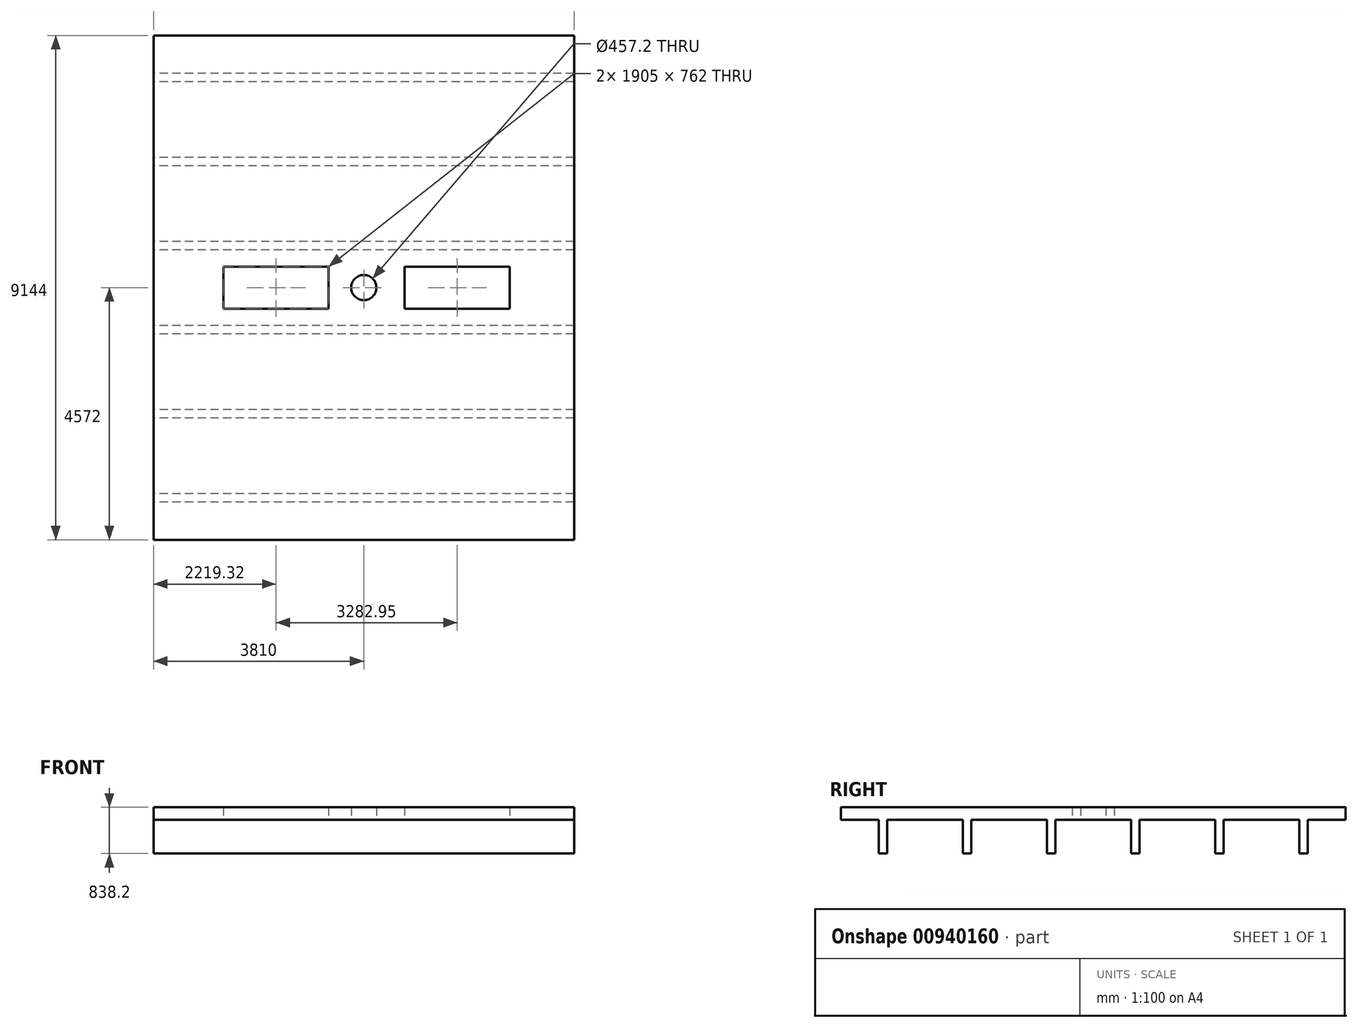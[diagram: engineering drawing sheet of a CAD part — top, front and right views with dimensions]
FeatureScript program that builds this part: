
annotation { "Feature Type Name" : "Feature", "Feature Type Description" : "" }
export const myFeature = defineFeature(function(context is Context, id is Id, definition is map)
    precondition{}
    {
        {
            var Q0;
            Q0=qCreatedBy(makeId("Top.planeOp"),FACE);
            var sketch = newSketch(context, id + "F0", { "sketchPlane" : qUnion([Q0])});
            skLineSegment(sketch, "E0.bottom", {"start": v(-3810, -4572) * mm, "end": v(3810, -4572) * mm});
            skLineSegment(sketch, "E0.top", {"start": v(-3810, 4572) * mm, "end": v(3810, 4572) * mm});
            skLineSegment(sketch, "E0.left", {"start": v(-3810, -4572) * mm, "end": v(-3810, 4572) * mm});
            skLineSegment(sketch, "E0.right", {"start": v(3810, -4572) * mm, "end": v(3810, 4572) * mm});
            skPoint(sketch, "E0.middle", {"position": v(0, 0) * mm});
            skCircle(sketch, "E1", {"center": v(0, 0) * mm, "radius": 228.6 * mm});
            skLineSegment(sketch, "E2.bottom", {"start": v(-2543.18, 381) * mm, "end": v(-638.17, 381) * mm});
            skLineSegment(sketch, "E2.top", {"start": v(-2543.18, -381) * mm, "end": v(-638.17, -381) * mm});
            skLineSegment(sketch, "E2.left", {"start": v(-2543.18, 381) * mm, "end": v(-2543.18, -381) * mm});
            skLineSegment(sketch, "E2.right", {"start": v(-638.18, 381) * mm, "end": v(-638.17, -381) * mm});
            skLineSegment(sketch, "E3.bottom", {"start": v(739.77, 381) * mm, "end": v(2644.78, 381) * mm});
            skLineSegment(sketch, "E3.top", {"start": v(739.78, -381) * mm, "end": v(2644.78, -381) * mm});
            skLineSegment(sketch, "E3.left", {"start": v(739.77, 381) * mm, "end": v(739.78, -381) * mm});
            skLineSegment(sketch, "E3.right", {"start": v(2644.78, 381) * mm, "end": v(2644.78, -381) * mm});
            skLineSegment(sketch, "E4", {"start": v(739.78, 0) * mm, "end": v(0, 0) * mm, "construction": true});
            skLineSegment(sketch, "E5", {"start": v(0, 0) * mm, "end": v(-638.17, 0) * mm, "construction": true});
            skLineSegment(sketch, "E6", {"start": v(0, 0) * mm, "end": v(0, 0) * mm});
            skSolve(sketch);
        }
        {
            var Q0;
            Q0=makeQuery(id+"F0.imprint","IMPRINT",FACE,{"disambiguationData":[TD([[makeQuery(id+"F0.imprint","IMPRINT",EDGE,{"derivedFrom":sQuery(id+"F0.wireOp",EDGE,"E0.bottom")}),1.0]])]});
            extrude(context, id + "F1", {"entities" : qUnion([Q0]), "depth" : 228.6 * mm, "offsetDistance" : 25.4 * mm});
        }
        {
            var Q0;
            Q0=qCreatedBy(makeId("Right.planeOp"),FACE);
            var sketch = newSketch(context, id + "F2", { "sketchPlane" : qUnion([Q0])});
            skLineSegment(sketch, "E7", {"start": v(-685.8, 0) * mm, "end": v(685.8, 0) * mm, "construction": true});
            skLineSegment(sketch, "E8.bottom", {"start": v(-685.8, 0) * mm, "end": v(-838.2, 0) * mm});
            skLineSegment(sketch, "E8.top", {"start": v(-685.8, -609.6) * mm, "end": v(-838.2, -609.6) * mm});
            skLineSegment(sketch, "E8.left", {"start": v(-685.8, 0) * mm, "end": v(-685.8, -609.6) * mm});
            skLineSegment(sketch, "E8.right", {"start": v(-838.2, 0) * mm, "end": v(-838.2, -609.6) * mm});
            skLineSegment(sketch, "E9.bottom", {"start": v(685.8, 0) * mm, "end": v(838.2, 0) * mm});
            skLineSegment(sketch, "E9.top", {"start": v(685.8, -609.6) * mm, "end": v(838.2, -609.6) * mm});
            skLineSegment(sketch, "E9.left", {"start": v(685.8, 0) * mm, "end": v(685.8, -609.6) * mm});
            skLineSegment(sketch, "E9.right", {"start": v(838.2, 0) * mm, "end": v(838.2, -609.6) * mm});
            skLineSegment(sketch, "E10.1.0.0", {"start": v(2362.2, 0) * mm, "end": v(2209.8, 0) * mm});
            skLineSegment(sketch, "E10.1.0.1", {"start": v(2209.8, 0) * mm, "end": v(2209.8, -609.6) * mm});
            skLineSegment(sketch, "E10.1.0.2", {"start": v(2362.2, 0) * mm, "end": v(2362.2, -609.6) * mm});
            skLineSegment(sketch, "E10.1.0.3", {"start": v(2362.2, -609.6) * mm, "end": v(2209.8, -609.6) * mm});
            skLineSegment(sketch, "E10.1.0.4", {"start": v(3886.2, 0) * mm, "end": v(3886.2, -609.6) * mm});
            skLineSegment(sketch, "E10.1.0.5", {"start": v(3733.8, 0) * mm, "end": v(3733.8, -609.6) * mm});
            skLineSegment(sketch, "E10.1.0.6", {"start": v(3733.8, -609.6) * mm, "end": v(3886.2, -609.6) * mm});
            skLineSegment(sketch, "E10.1.0.7", {"start": v(3733.8, 0) * mm, "end": v(3886.2, 0) * mm});
            skLineSegment(sketch, "E10.direction1", {"start": v(-838.2, -609.6) * mm, "end": v(2209.8, -609.6) * mm, "construction": true});
            skLineSegment(sketch, "E11.1.0.0", {"start": v(-3733.8, 0) * mm, "end": v(-3886.2, 0) * mm});
            skLineSegment(sketch, "E11.1.0.1", {"start": v(-3733.8, -609.6) * mm, "end": v(-3886.2, -609.6) * mm});
            skLineSegment(sketch, "E11.1.0.2", {"start": v(-3733.8, 0) * mm, "end": v(-3733.8, -609.6) * mm});
            skLineSegment(sketch, "E11.1.0.3", {"start": v(-3886.2, 0) * mm, "end": v(-3886.2, -609.6) * mm});
            skLineSegment(sketch, "E11.1.0.4", {"start": v(-2362.2, 0) * mm, "end": v(-2209.8, 0) * mm});
            skLineSegment(sketch, "E11.1.0.5", {"start": v(-2362.2, -609.6) * mm, "end": v(-2209.8, -609.6) * mm});
            skLineSegment(sketch, "E11.1.0.6", {"start": v(-2362.2, 0) * mm, "end": v(-2362.2, -609.6) * mm});
            skLineSegment(sketch, "E11.1.0.7", {"start": v(-2209.8, 0) * mm, "end": v(-2209.8, -609.6) * mm});
            skLineSegment(sketch, "E11.direction1", {"start": v(-838.2, -609.6) * mm, "end": v(-3886.2, -609.6) * mm, "construction": true});
            skSolve(sketch);
        }
        {
            var Q0;
            Q0=qSketchRegion(id+"F2",true);
            var Q1;
            Q1=makeQuery(id+"F1.opExtrude","SWEPT_FACE",FACE,{"disambiguationData":[OSD([sQuery(id+"F0.wireOp",EDGE,"E0.right")])]});
            var Q2;
            Q2=makeQuery(id+"F1.opExtrude","SWEPT_FACE",FACE,{"disambiguationData":[OSD([sQuery(id+"F0.wireOp",EDGE,"E0.left")])]});
            extrude(context, id + "F3", {"entities" : qUnion([Q0]), "operationType" : NewBodyOperationType.ADD, "endBound" : BoundingType.UP_TO_SURFACE, "depth" : 25.4 * mm, "endBoundEntityFace" : qUnion([Q1]), "offsetDistance" : 25.4 * mm, "hasSecondDirection" : true, "secondDirectionBound" : SecondDirectionBoundingType.UP_TO_SURFACE, "secondDirectionOppositeDirection" : true, "secondDirectionDepth" : 25.4 * mm, "secondDirectionBoundEntityFace" : qUnion([Q2])});
        }
    });
